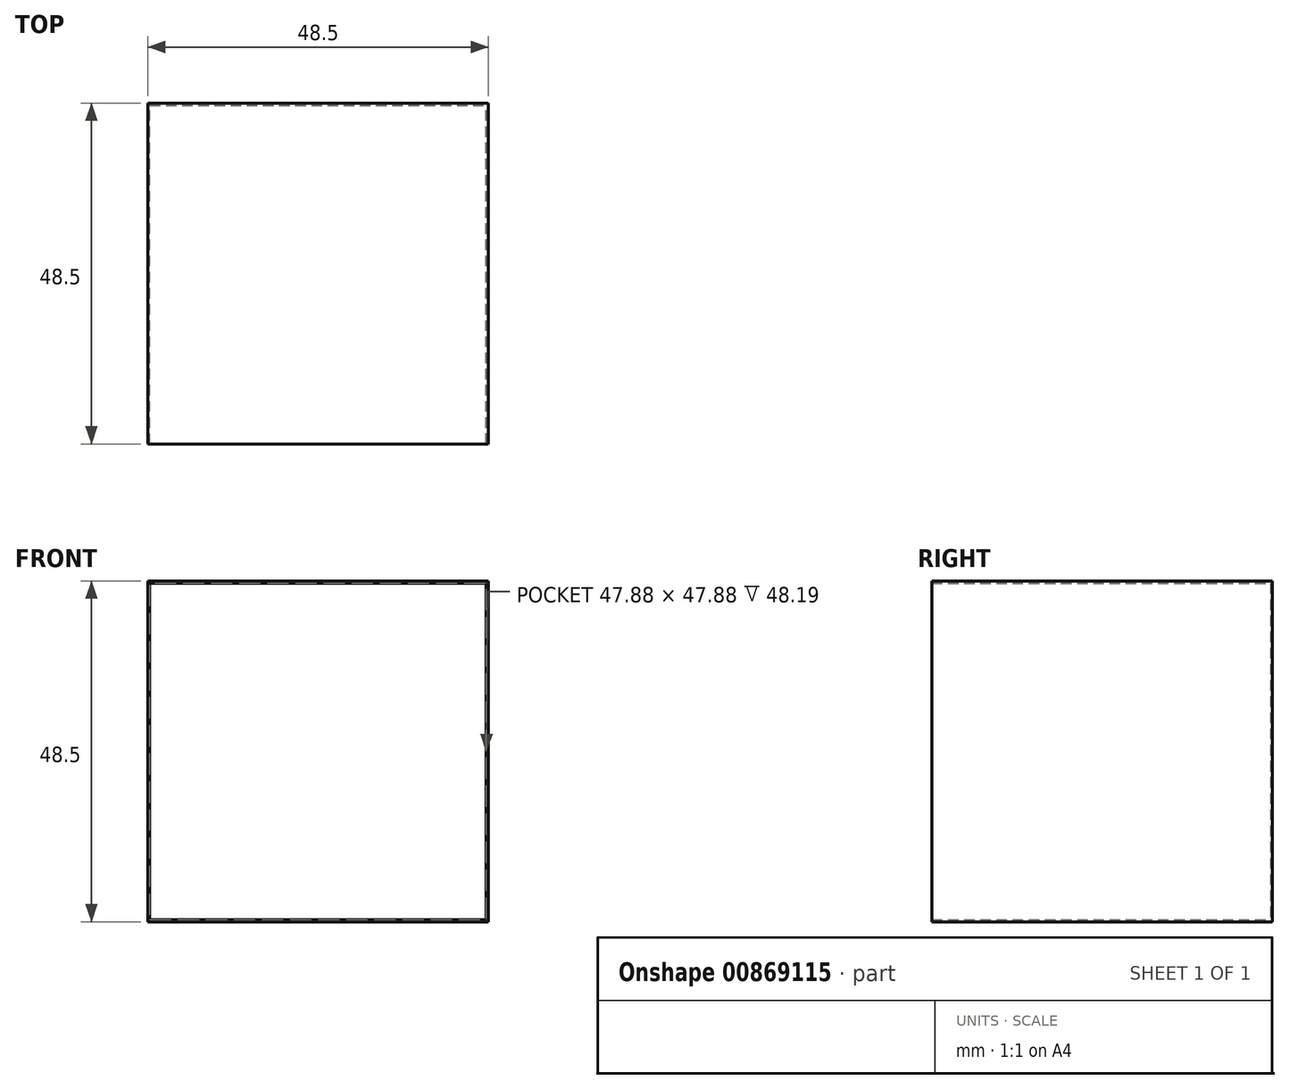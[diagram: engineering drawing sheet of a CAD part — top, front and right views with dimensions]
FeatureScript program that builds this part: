
annotation { "Feature Type Name" : "Feature", "Feature Type Description" : "" }
export const myFeature = defineFeature(function(context is Context, id is Id, definition is map)
    precondition{}
    {
        {
            assignVariable(context, id + "F0", {"name" : "size", "anyValue" : 48.5});
        }
        {
            assignVariable(context, id + "F1", {"name" : "thickness", "anyValue" : 0.31});
        }
        {
            var Q0;
            Q0=qCreatedBy(makeId("Front.planeOp"),FACE);
            var sketch = newSketch(context, id + "F2", { "sketchPlane" : qUnion([Q0])});
            skLineSegment(sketch, "E0.bottom", {"start": v(-413.42, -617.06) * mm, "end": v(-364.92, -617.06) * mm});
            skLineSegment(sketch, "E0.top", {"start": v(-413.42, -665.56) * mm, "end": v(-364.92, -665.56) * mm});
            skLineSegment(sketch, "E0.left", {"start": v(-413.42, -617.06) * mm, "end": v(-413.42, -665.56) * mm});
            skLineSegment(sketch, "E0.right", {"start": v(-364.92, -665.56) * mm, "end": v(-364.92, -617.06) * mm});
            skLineSegment(sketch, "E1.bottom", {"start": v(-413.1, -617.37) * mm, "end": v(-365.23, -617.37) * mm});
            skLineSegment(sketch, "E1.top", {"start": v(-413.1, -665.25) * mm, "end": v(-365.23, -665.25) * mm});
            skLineSegment(sketch, "E1.left", {"start": v(-413.1, -617.37) * mm, "end": v(-413.1, -665.25) * mm});
            skLineSegment(sketch, "E1.right", {"start": v(-365.23, -617.37) * mm, "end": v(-365.23, -665.25) * mm});
            skSolve(sketch);
        }
        {
            var Q0;
            Q0=makeQuery(id+"F2.imprint","IMPRINT",FACE,{"disambiguationData":[TD([[makeQuery(id+"F2.imprint","IMPRINT",EDGE,{"derivedFrom":sQuery(id+"F2.wireOp",EDGE,"E1.bottom")}),-1.0]])]});
            extrude(context, id + "F3", {"entities" : qUnion([Q0]), "depth" : (getVariable(context, 'thickness')) * mm, "offsetDistance" : 25 * mm});
        }
        {
            var Q0;
            Q0 = qSketchRegion(id + "F2", true);
            extrude(context, id + "F4", {"entities" : qUnion([Q0]), "operationType" : NewBodyOperationType.ADD, "depth" : (getVariable(context, 'size')) * mm, "offsetDistance" : 25 * mm});
        }
    });
